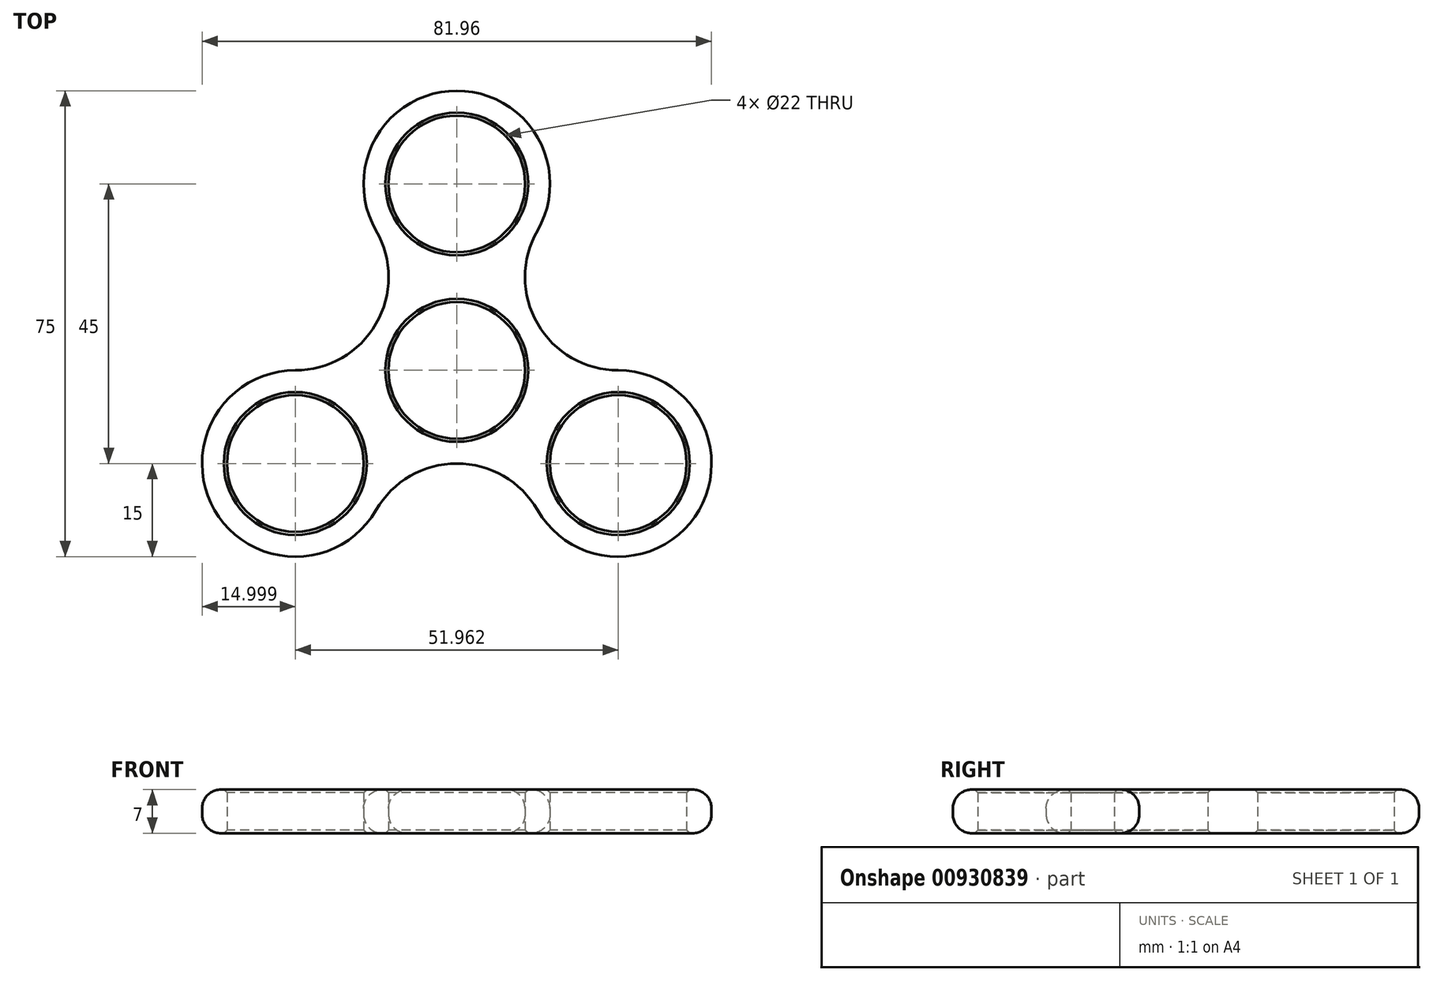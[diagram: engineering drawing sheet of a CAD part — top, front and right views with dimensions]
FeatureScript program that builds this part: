
annotation { "Feature Type Name" : "Feature", "Feature Type Description" : "" }
export const myFeature = defineFeature(function(context is Context, id is Id, definition is map)
    precondition{}
    {
        {
            assignVariable(context, id + "F0", {"name" : "thk", "anyValue" : 7});
        }
        {
            var Q0;
            Q0=qCreatedBy(makeId("Top.planeOp"),FACE);
            var sketch = newSketch(context, id + "F1", { "sketchPlane" : qUnion([Q0])});
            skCircle(sketch, "E0", {"center": v(0, 30) * mm, "radius": 11 * mm});
            skCircle(sketch, "E1", {"center": v(0, 30) * mm, "radius": 15 * mm});
            skCircle(sketch, "E2", {"center": v(0, 0) * mm, "radius": 11 * mm});
            skCircle(sketch, "E3.1.0", {"center": v(-25.98, -15) * mm, "radius": 15 * mm});
            skCircle(sketch, "E3.1.1", {"center": v(-25.98, -15) * mm, "radius": 11 * mm});
            skCircle(sketch, "E3.2.0", {"center": v(25.98, -15) * mm, "radius": 15 * mm});
            skCircle(sketch, "E3.2.1", {"center": v(25.98, -15) * mm, "radius": 11 * mm});
            skArc(sketch, "E4", {"start": v(13, 22.5) * mm, "mid": v(13, 7.5) * mm, "end": v(25.98, 0) * mm});
            skArc(sketch, "E5.1.0", {"start": v(-25.98, 0) * mm, "mid": v(-13, 7.5) * mm, "end": v(-13, 22.5) * mm});
            skArc(sketch, "E5.2.0", {"start": v(13, -22.5) * mm, "mid": v(0, -15) * mm, "end": v(-13, -22.5) * mm});
            skSolve(sketch);
        }
        {
            var Q0;
            Q0=makeQuery(id+"F1.imprint","IMPRINT",FACE,{"disambiguationData":[TD([[makeQuery(id+"F1.imprint","IMPRINT",EDGE,{"derivedFrom":sQuery(id+"F1.wireOp",EDGE,"E3.1.1")}),-1.0]])]});
            var Q1;
            Q1=makeQuery(id+"F1.imprint","IMPRINT",FACE,{"disambiguationData":[TD([[makeQuery(id+"F1.imprint","IMPRINT",EDGE,{"derivedFrom":sQuery(id+"F1.wireOp",EDGE,"E3.2.1")}),-1.0]])]});
            var Q2;
            Q2=makeQuery(id+"F1.imprint","IMPRINT",FACE,{"disambiguationData":[TD([[makeQuery(id+"F1.imprint","IMPRINT",EDGE,{"derivedFrom":sQuery(id+"F1.wireOp",EDGE,"E2")}),-1.0]])]});
            var Q3;
            Q3=makeQuery(id+"F1.imprint","IMPRINT",FACE,{"disambiguationData":[TD([[makeQuery(id+"F1.imprint","IMPRINT",EDGE,{"derivedFrom":sQuery(id+"F1.wireOp",EDGE,"E0")}),-1.0]])]});
            extrude(context, id + "F2", {"entities" : qUnion([Q0, Q1, Q2, Q3]), "depth" : (getVariable(context, 'thk')) * mm, "offsetDistance" : 25 * mm});
        }
        {
            var Q0;
            Q0=makeQuery(id+"F2.opExtrude","CAP_EDGE",EDGE,{"disambiguationData":[OSD([sQuery(id+"F1.wireOp",EDGE,"E5.2.0")])],"isStart":false});
            var Q1;
            Q1=makeQuery(id+"F2.opExtrude","CAP_EDGE",EDGE,{"disambiguationData":[OSD([sQuery(id+"F1.wireOp",EDGE,"E3.1.0")])],"isStart":false});
            var Q2;
            Q2=makeQuery(id+"F2.opExtrude","CAP_EDGE",EDGE,{"disambiguationData":[OSD([sQuery(id+"F1.wireOp",EDGE,"E5.2.0")])],"isStart":true});
            fillet(context, id + "F3", {"entities" : qUnion([Q0, Q1, Q2]), "radius" : 3 * mm, "tangentPropagation" : true, "allowEdgeOverflow" : false});
        }
        {
            var Q0;
            Q0=makeQuery(id+"F2.opExtrude","SWEPT_FACE",FACE,{"disambiguationData":[OSD([sQuery(id+"F1.wireOp",EDGE,"E2")])]});
            var Q1;
            Q1=makeQuery(id+"F2.opExtrude","SWEPT_FACE",FACE,{"disambiguationData":[OSD([sQuery(id+"F1.wireOp",EDGE,"E0")])]});
            var Q2;
            Q2=makeQuery(id+"F2.opExtrude","SWEPT_FACE",FACE,{"disambiguationData":[OSD([sQuery(id+"F1.wireOp",EDGE,"E3.2.1")])]});
            var Q3;
            Q3=makeQuery(id+"F2.opExtrude","SWEPT_FACE",FACE,{"disambiguationData":[OSD([sQuery(id+"F1.wireOp",EDGE,"E3.1.1")])]});
            chamfer(context, id + "F4", {"entities" : qUnion([Q0, Q1, Q2, Q3]), "width" : 0.5 * mm, "tangentPropagation" : true});
        }
    });
